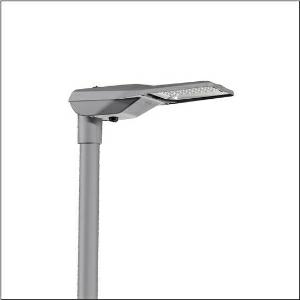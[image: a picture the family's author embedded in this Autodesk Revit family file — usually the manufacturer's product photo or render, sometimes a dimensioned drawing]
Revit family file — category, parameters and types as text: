
# Revit family: streetlight_sl_21_mini___st0_5a_5xe2b43t08jb_6bf0
name_source: partatom
category: Lighting Fixtures
units: mm (PartAtom-declared; Revit-internal decimal feet)

## family parameters
Cut with Voids When Loaded = No
Host = Face
Light Source = No
Part Type = Normal
Room Calculation Point = No
Round Connector Dimension = Use Diameter
Shared = No

## types (1)
- --- (1 x LED, 13500 lm, 88.6 W, 4000K)
    Apparent Load = 89 VA
    CIE Flux Codes = 43 76 97 100 100
    Color Rendering = 70
    Color Temperature = 4000K
    Default Elevation = 1800 mm
    Description = Streetlight SL 21 mini, mast luminaire, primary light control with lens, of PMMA, primary optical cover: cover, of toughened safety glass, transparent, light distribution: ST0.5a, light emission: direct distribution, primary light characteristic: asymmetric, installation type: side-entry, post-top, LED, High Power LED, rated luminous flux: 13.500lm, luminous efficacy: 152lm/W, light colour: 740, colour temperature: 4000K, control gear: D4i, control: overheat protection, constant luminous flux control, time-dependent luminous flux control, flexible luminous flux parameterisation, pre-setting: logarithmic dimming characteristic, mains connection: 220..240V, AC, 50/60Hz, start of lifetime: 89W, end of service life: 92W, reduction: 41W, luminaire housing, of diecast aluminium, powder-coated, Siteco® metallic grey (DB 702S), corrosivity category C5 mid according to DIN EN ISO 12944, please order mast flange separately, inclination adjustable: 0°, 5°, 10°, 15°, sealing non-destructively replaceable, multi-level sealing system, length: 628mm, width: 235mm, height: 110mm, mast flange for spigot size: 42mm (side-entry): 5XC10008XM4, 60/48mm (side-entry/post-top): 5XC10108XM2, 76/60mm (side-entry/post-top): 5XC10108XM1, mounting height: 4..8m, Smart Interface below and above, protection rating (complete): IP66, insulation class (complete): insulation class II (safety insulation), certification: CE, ENEC, ENEC+, VDE, impact resistance: IK10, permissible operating ambient temperature for outdoor applications: -40..+50°C, standard-compliant lighting for roads and squares, packaging unit: 1 piece

Light Distribution: ST0.5a
    Height = 110 mm
    Lamp = 1 x LED
    Lamp Light Flux = 13500 lm
    Lamp Power = 88.6 W
    Lamp count = 1
    Length = 625 mm
    Luminous efficacy = 152 lm/W
    Manufacturer = Siteco
    ModVariant = No
    Model = 5XE2B43T08JB
    Number of Poles = 1
    OnlyDefault = Yes
    Power Factor = 1
    Product Name = Streetlight SL 21 mini | ST0.5a
    Product group = mast luminaire | pylon top
    ProductGroupID = 6100
    Protection Class = Protection class II
    Protection Degree = IP 66
    RLX_Detail_Level = 1
    RLX_Emergency_Light_Flux = 0 lm
    RLX_Emergency_Type = 0
    RLX_Emergency_Type_DB = No
    RlxData = <blob elided: 37569 chars, md5=ea0a1d26>
    Socket = socket
    Standby Power = 0 W
    System Light Flux = 13500 lm
    System Power = 89 W
    Type Comments = factory setting: luminous flux: 100 % | dim-lin: 254 | 915 mA
    Type Image = l_1003514.jpg
    URL = http://relux.com
    VarID = @adj_012403
    Voltage = 0 V
    Weight = 0.00 kg
    Width = 234 mm

## geometry (parser evidence)
native form markers: Blend x4, Sweep x11
no freeform markers — native parametric forms only
